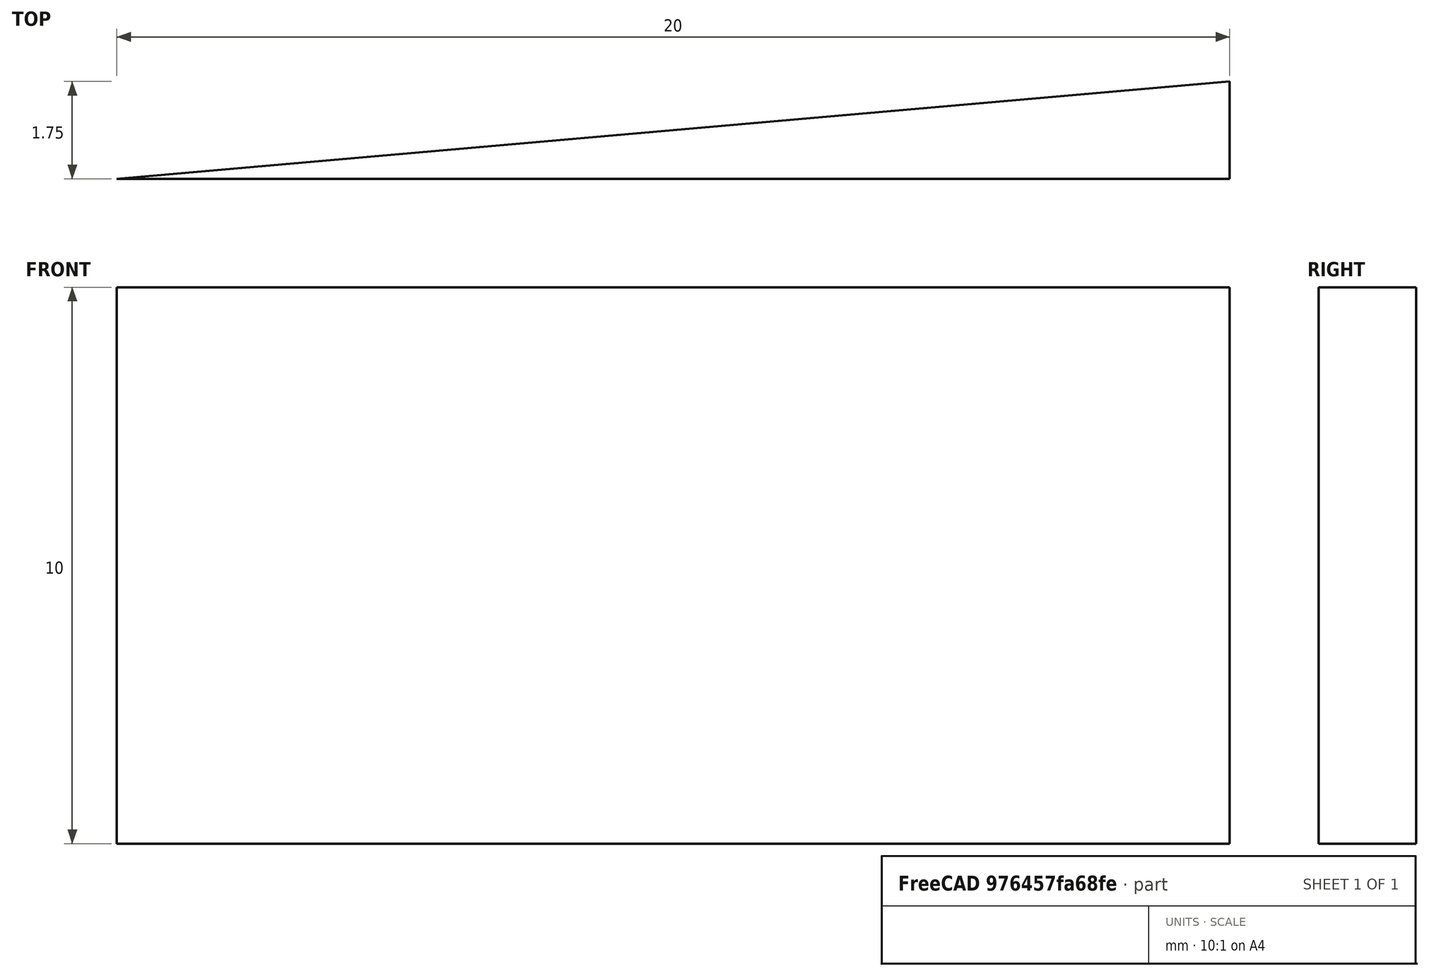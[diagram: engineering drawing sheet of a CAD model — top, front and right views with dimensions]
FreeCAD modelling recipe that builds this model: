
FCSTD DOCUMENT  (FreeCAD 0.18R16110 (Git))
Label: layer_height_wedge
License: All rights reserved
LicenseURL: http://en.wikipedia.org/wiki/All_rights_reserved
objects: Sketcher::SketchObject×1, App::Part×1, Part::Extrusion×1
note: 2 computed .brp shape members not serialized (recipe doc carries the construction recipe); baked Part::Feature solids carry a one-line shape summary decoded from their .brp

FEATURE [Sketcher::SketchObject] Sketch
  sketch-geometry (3):
    g0: LineSegment StartX=0 StartY=0 StartZ=0 EndX=20 EndY=1.74977 EndZ=0
    g1: LineSegment StartX=20 StartY=1.74977 StartZ=0 EndX=20 EndY=0 EndZ=0
    g2: LineSegment StartX=20 StartY=0 StartZ=0 EndX=0 EndY=0 EndZ=0
  constraints (8):
    c: Perpendicular(g2,g1)
    c: Angle(g2,g0) = 0.0872665
    c: Coincident(g0,g-1)
    c: Coincident(g2,g0)
    c: Coincident(g0,g1)
    c: Coincident(g1,g2)
    c: Angle(g-1,g2) = 0
    c: Distance(g2) = 20
FEATURE [App::Part] Part
  Origin = -> Origin
FEATURE [Part::Extrusion] Extrude
  Base = -> Sketch
  Dir = (0,0,1)
  DirMode = 2
  FaceMakerClass = Part::FaceMakerBullseye
  LengthFwd = 10
  LengthRev = 0
  Solid = true
  Symmetric = false
